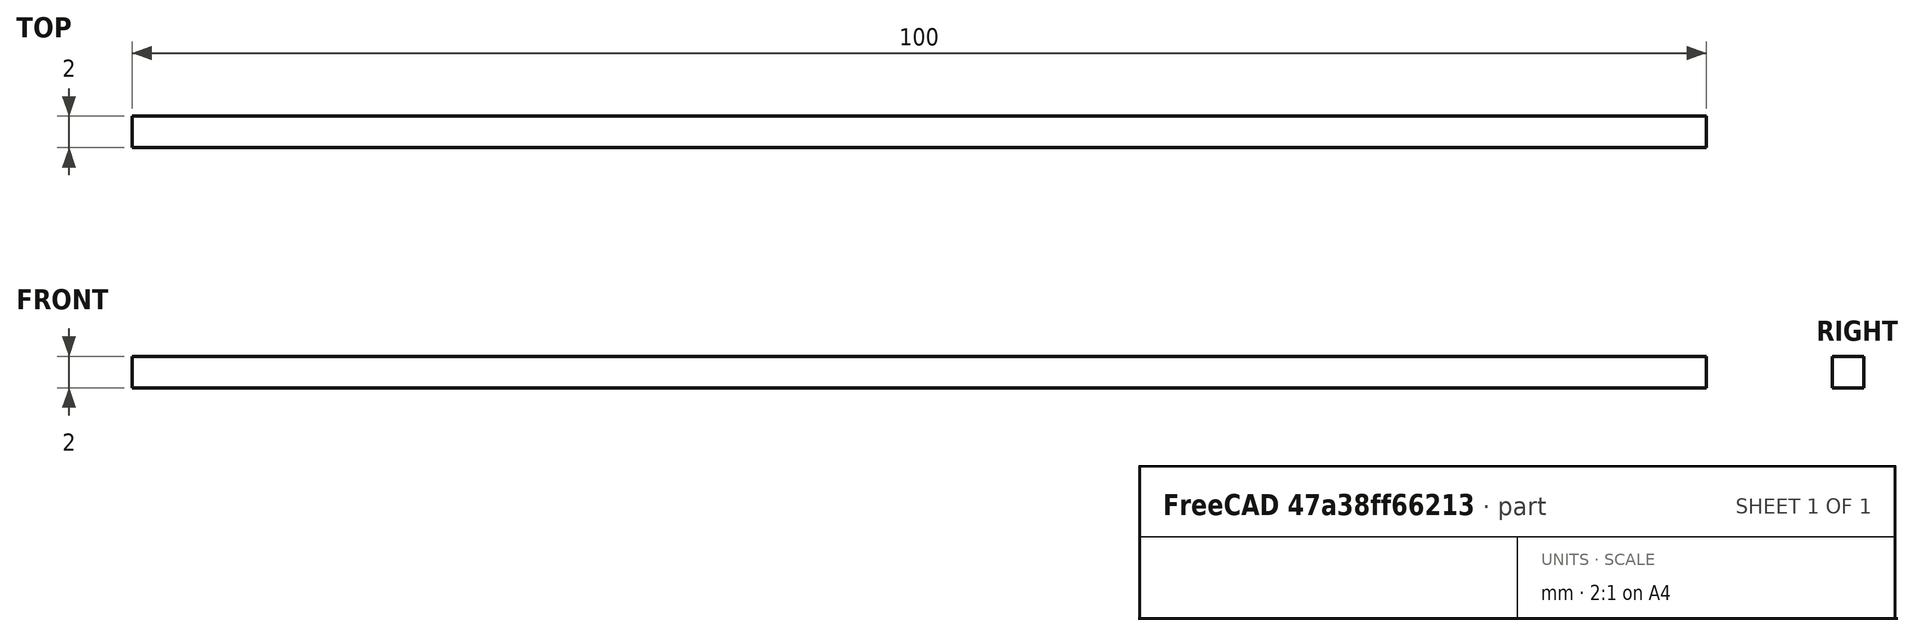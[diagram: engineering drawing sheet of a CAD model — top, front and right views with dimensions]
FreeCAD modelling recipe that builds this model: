
FCSTD DOCUMENT  (FreeCAD 0.18.1R)
Label: rod balloon techdraw
License: All rights reserved
LicenseURL: http://en.wikipedia.org/wiki/All_rights_reserved
objects: TechDraw::DrawProjGroupItem×4, TechDraw::DrawSVGTemplate×2, TechDraw::DrawPage×2, TechDraw::DrawViewDimension×2, Part::Box×1, TechDraw::DrawProjGroup×1
note: 1 computed .brp shape members not serialized (recipe doc carries the construction recipe); baked Part::Feature solids carry a one-line shape summary decoded from their .brp

FEATURE [Part::Box] Box  label="Cube"
  AttacherType = Attacher::AttachEngine3D
  Height = 2
  Length = 100
  Width = 2
FEATURE [TechDraw::DrawSVGTemplate] Template
  EditableTexts = Designed_by_Name=Designed by Name; Drawing_number=Drawing number; FC-Date=Date; FC-SC=Scale; FC-SH=Sheet; FC-Title=Title; Subtitle=Subtitle; Weight=Weight
  Height = 210
  Orientation = 1
  Width = 297
FEATURE [TechDraw::DrawPage] Page
  KeepUpdated = true
  ProjectionType = 0
  Template = -> Template
FEATURE [TechDraw::DrawSVGTemplate] Template001
  EditableTexts = Designed_by_Name=Designed by Name; Drawing_number=Drawing number; FC-Date=Date; FC-SC=Scale; FC-SH=Sheet; FC-Title=Title; Subtitle=Subtitle; Weight=Weight
  Height = 210
  Orientation = 1
  Width = 297
FEATURE [TechDraw::DrawProjGroupItem] ProjItem  label="Front"
  CoarseView = false
  Direction = (0,-1,0)
  Focus = 100
  HardHidden = false
  IsoCount = 0
  IsoHidden = false
  IsoVisible = false
  LockPosition = true
  Perspective = false
  Rotation = 0
  RotationVector = (1,0,0)
  ScaleType = 2
  SeamHidden = false
  SeamVisible = false
  SmoothHidden = false
  SmoothVisible = false
  Source = -> [Box]
  Type = 0
  X = 0
  Y = 0
FEATURE [TechDraw::DrawProjGroupItem] ProjItem001  label="Left"
  CoarseView = false
  Direction = (-1,-1e-16,0)
  Focus = 100
  HardHidden = false
  IsoCount = 0
  IsoHidden = false
  IsoVisible = false
  LockPosition = false
  Perspective = false
  Rotation = 0
  RotationVector = (1e-16,-1,0)
  ScaleType = 2
  SeamHidden = false
  SeamVisible = false
  SmoothHidden = false
  SmoothVisible = false
  Source = -> [Box]
  Type = 1
  X = 98.1087
  Y = 0
FEATURE [TechDraw::DrawProjGroupItem] ProjItem002  label="FrontTopLeft"
  CoarseView = false
  Direction = (-1,-1,1)
  Focus = 100
  HardHidden = false
  IsoCount = 0
  IsoHidden = false
  IsoVisible = false
  LockPosition = false
  Perspective = false
  Rotation = 0
  RotationVector = (1,-1,0)
  ScaleType = 2
  SeamHidden = false
  SeamVisible = false
  SmoothHidden = false
  SmoothVisible = false
  Source = -> [Box]
  Type = 6
  X = 124.725
  Y = -72.0039
FEATURE [TechDraw::DrawProjGroupItem] ProjItem003  label="Top"
  CoarseView = false
  Direction = (0,0,1)
  Focus = 100
  HardHidden = false
  IsoCount = 0
  IsoHidden = false
  IsoVisible = false
  LockPosition = false
  Perspective = false
  Rotation = 0
  RotationVector = (1,0,0)
  ScaleType = 2
  SeamHidden = false
  SeamVisible = false
  SmoothHidden = false
  SmoothVisible = false
  Source = -> [Box]
  Type = 4
  X = 0
  Y = -73.5395
FEATURE [TechDraw::DrawProjGroup] ProjGroup
  Anchor = -> ProjItem
  AutoDistribute = true
  LockPosition = false
  ProjectionType = 1
  Rotation = 0
  ScaleType = 0
  Source = -> [Box]
  Views = -> [ProjItem,ProjItem001,ProjItem002,ProjItem003]
  X = 83.8623
  Y = 175.479
  spacingX = 15
  spacingY = 15
FEATURE [TechDraw::DrawViewDimension] Dimension
  Arbitrary = false
  FormatSpec = %.2f
  LockPosition = false
  MeasureType = 1
  OverTolerance = 0
  References2D = -> [ProjItem]
  Rotation = 0
  ScaleType = 0
  Type = 1
  UnderTolerance = 0
  X = 5.62807
  Y = -15.2183
FEATURE [TechDraw::DrawViewDimension] Dimension001
  Arbitrary = false
  FormatSpec = %.2f
  LockPosition = false
  MeasureType = 1
  OverTolerance = 0
  References2D = -> [ProjItem001]
  Rotation = 0
  ScaleType = 0
  Type = 2
  UnderTolerance = 0
  X = 27.1627
  Y = -0.187782
FEATURE [TechDraw::DrawPage] Page001
  KeepUpdated = true
  ProjectionType = 0
  Template = -> Template001
  Views = -> [ProjGroup,Dimension,Dimension001]
